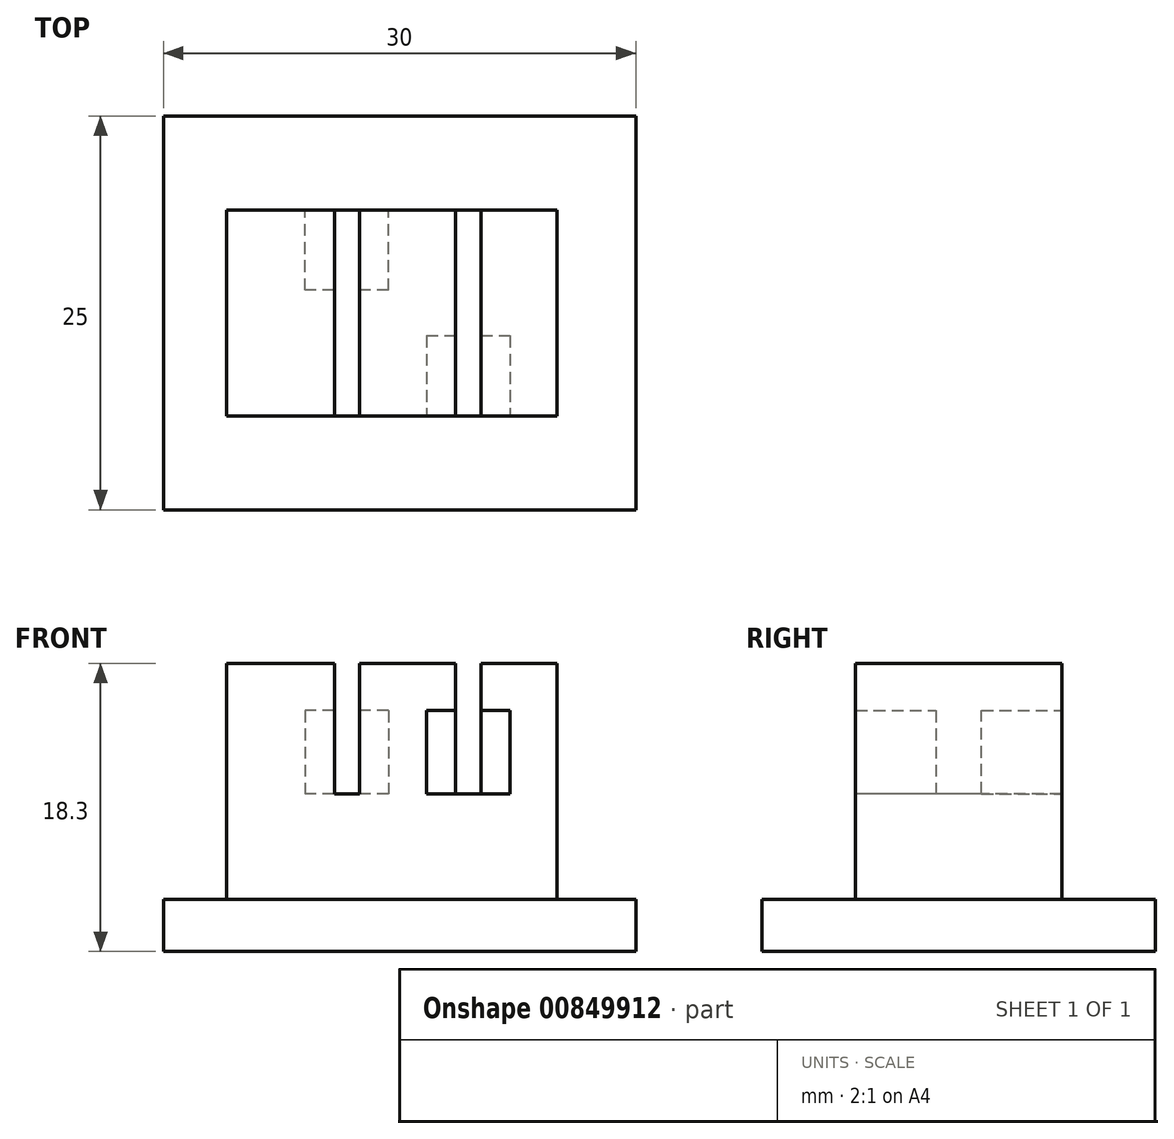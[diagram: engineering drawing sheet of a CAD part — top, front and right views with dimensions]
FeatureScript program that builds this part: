
annotation { "Feature Type Name" : "Feature", "Feature Type Description" : "" }
export const myFeature = defineFeature(function(context is Context, id is Id, definition is map)
    precondition{}
    {
        {
            var Q0;
            Q0=qCreatedBy(makeId("Top.planeOp"),FACE);
            var sketch = newSketch(context, id + "F0", { "sketchPlane" : qUnion([Q0])});
            skLineSegment(sketch, "E0.bottom", {"start": v(-15, 12.5) * mm, "end": v(15, 12.5) * mm});
            skLineSegment(sketch, "E0.top", {"start": v(-15, -12.5) * mm, "end": v(15, -12.5) * mm});
            skLineSegment(sketch, "E0.left", {"start": v(-15, 12.5) * mm, "end": v(-15, -12.5) * mm});
            skLineSegment(sketch, "E0.right", {"start": v(15, 12.5) * mm, "end": v(15, -12.5) * mm});
            skSolve(sketch);
        }
        {
            var Q0;
            Q0=makeQuery(id+"F0.imprint","IMPRINT",FACE,{"disambiguationData":[TD([[makeQuery(id+"F0.imprint","IMPRINT",EDGE,{"derivedFrom":sQuery(id+"F0.wireOp",EDGE,"E0.bottom")}),-1.0]])]});
            var Q1;
            Q1 = qSketchRegion(id + "F2", true);
            extrude(context, id + "F1", {"entities" : qUnion([Q0, Q1]), "depth" : 3.3 * mm, "offsetDistance" : 25 * mm});
        }
        {
            var Q0;
            Q0=makeQuery(id+"F1.opExtrude","CAP_FACE",FACE,{"disambiguationData":[OSD([sQuery(id+"F0.wireOp",EDGE,"E0.bottom"),sQuery(id+"F0.wireOp",EDGE,"E0.top"),sQuery(id+"F0.wireOp",EDGE,"E0.left"),sQuery(id+"F0.wireOp",EDGE,"E0.right")])],"isStart":false});
            var sketch = newSketch(context, id + "F2", { "sketchPlane" : qUnion([Q0])});
            skLineSegment(sketch, "E1.bottom", {"start": v(-11, 6.55) * mm, "end": v(10, 6.55) * mm});
            skLineSegment(sketch, "E1.top", {"start": v(-11, -6.55) * mm, "end": v(10, -6.55) * mm});
            skLineSegment(sketch, "E1.left", {"start": v(-11, 6.55) * mm, "end": v(-11, -6.55) * mm});
            skLineSegment(sketch, "E1.right", {"start": v(10, 6.55) * mm, "end": v(10, -6.55) * mm});
            skLineSegment(sketch, "E2", {"start": v(-11, -6.55) * mm, "end": v(-15, -6.55) * mm});
            skLineSegment(sketch, "E3", {"start": v(10, 6.55) * mm, "end": v(10, 12.5) * mm});
            skLineSegment(sketch, "E4", {"start": v(-11, -6.55) * mm, "end": v(-11, -12.5) * mm});
            skSolve(sketch);
        }
        {
            var Q0;
            Q0=makeQuery(id+"F2.imprint","IMPRINT",FACE,{"disambiguationData":[TD([[makeQuery(id+"F2.imprint","IMPRINT",EDGE,{"derivedFrom":sQuery(id+"F2.wireOp",EDGE,"E1.bottom")}),-1.0]])]});
            extrude(context, id + "F3", {"entities" : qUnion([Q0]), "operationType" : NewBodyOperationType.ADD, "depth" : 15 * mm, "offsetDistance" : 25 * mm});
        }
        {
            var Q0;
            Q0=makeQuery(id+"F3.opExtrude","SWEPT_FACE",FACE,{"disambiguationData":[OSD([sQuery(id+"F2.wireOp",EDGE,"E1.top")])]});
            var sketch = newSketch(context, id + "F4", { "sketchPlane" : qUnion([Q0])});
            skLineSegment(sketch, "E5.bottom", {"start": v(1.7, 15.3) * mm, "end": v(7, 15.3) * mm});
            skLineSegment(sketch, "E5.top", {"start": v(1.7, 10) * mm, "end": v(7, 10) * mm});
            skLineSegment(sketch, "E5.left", {"start": v(1.7, 15.3) * mm, "end": v(1.7, 10) * mm});
            skLineSegment(sketch, "E5.right", {"start": v(7, 15.3) * mm, "end": v(7, 10) * mm});
            skLineSegment(sketch, "E6", {"start": v(1.7, 15.3) * mm, "end": v(1.7, 18.3) * mm});
            skLineSegment(sketch, "E7", {"start": v(7, 15.3) * mm, "end": v(10, 15.3) * mm});
            skSolve(sketch);
        }
        {
            var Q0;
            Q0 = qSketchRegion(id + "F4", true);
            var Q1;
            Q1=makeQuery(id+"F4.imprint","IMPRINT",FACE,{"disambiguationData":[TD([[makeQuery(id+"F4.imprint","IMPRINT",EDGE,{"derivedFrom":sQuery(id+"F4.wireOp",EDGE,"E5.bottom")}),-1.0]])]});
            extrude(context, id + "F5", {"entities" : qUnion([Q0, Q1]), "operationType" : NewBodyOperationType.REMOVE, "oppositeDirection" : true, "depth" : 5.1 * mm, "offsetDistance" : 25 * mm});
        }
        {
            var Q0;
            Q0=makeQuery(id+"F3.opExtrude","CAP_FACE",FACE,{"disambiguationData":[OSD([sQuery(id+"F2.wireOp",EDGE,"E1.bottom"),sQuery(id+"F2.wireOp",EDGE,"E1.top"),sQuery(id+"F2.wireOp",EDGE,"E1.left"),sQuery(id+"F2.wireOp",EDGE,"E1.right")])],"isStart":false});
            var sketch = newSketch(context, id + "F6", { "sketchPlane" : qUnion([Q0])});
            skLineSegment(sketch, "E8.bottom", {"start": v(3.55, 6.55) * mm, "end": v(5.15, 6.55) * mm});
            skLineSegment(sketch, "E8.top", {"start": v(3.55, -6.55) * mm, "end": v(5.15, -6.55) * mm});
            skLineSegment(sketch, "E8.left", {"start": v(3.55, 6.55) * mm, "end": v(3.55, -6.55) * mm});
            skLineSegment(sketch, "E8.right", {"start": v(5.15, 6.55) * mm, "end": v(5.15, -6.55) * mm});
            skLineSegment(sketch, "E9", {"start": v(5.15, -6.55) * mm, "end": v(10, -6.55) * mm});
            skSolve(sketch);
        }
        {
            var Q0;
            Q0=makeQuery(id+"F6.imprint","IMPRINT",FACE,{"disambiguationData":[TD([[makeQuery(id+"F6.imprint","IMPRINT",EDGE,{"derivedFrom":sQuery(id+"F6.wireOp",EDGE,"E8.bottom")}),-1.0]])]});
            extrude(context, id + "F7", {"entities" : qUnion([Q0]), "operationType" : NewBodyOperationType.REMOVE, "oppositeDirection" : true, "depth" : 8.3 * mm, "offsetDistance" : 25 * mm});
        }
        {
            var Q0;
            Q0=makeQuery(id+"F3.opExtrude","SWEPT_FACE",FACE,{"disambiguationData":[OSD([sQuery(id+"F2.wireOp",EDGE,"E1.bottom")])]});
            var sketch = newSketch(context, id + "F8", { "sketchPlane" : qUnion([Q0])});
            skLineSegment(sketch, "E10.bottom", {"start": v(0.7, 15.3) * mm, "end": v(6, 15.3) * mm});
            skLineSegment(sketch, "E10.top", {"start": v(0.7, 10) * mm, "end": v(6, 10) * mm});
            skLineSegment(sketch, "E10.left", {"start": v(0.7, 15.3) * mm, "end": v(0.7, 10) * mm});
            skLineSegment(sketch, "E10.right", {"start": v(6, 15.3) * mm, "end": v(6, 10) * mm});
            skLineSegment(sketch, "E11", {"start": v(6, 15.3) * mm, "end": v(11, 15.3) * mm});
            skLineSegment(sketch, "E12", {"start": v(6, 15.3) * mm, "end": v(6, 18.3) * mm});
            skSolve(sketch);
        }
        {
            var Q0;
            Q0=makeQuery(id+"F8.imprint","IMPRINT",FACE,{"disambiguationData":[TD([[makeQuery(id+"F8.imprint","IMPRINT",EDGE,{"derivedFrom":sQuery(id+"F8.wireOp",EDGE,"E10.bottom")}),-1.0]])]});
            extrude(context, id + "F9", {"entities" : qUnion([Q0]), "operationType" : NewBodyOperationType.REMOVE, "oppositeDirection" : true, "depth" : 5.1 * mm, "offsetDistance" : 25 * mm});
        }
        {
            var Q0;
            {var subQ0=sQuery(id+"F2.wireOp",EDGE,"E1.bottom");var subQ1=sQuery(id+"F2.wireOp",EDGE,"E1.top");var subQ2=sQuery(id+"F2.wireOp",EDGE,"E1.left");Q0=makeQuery(id+"F7.boolean.opBoolean","SPLIT",FACE,{"disambiguationData":[TD([makeQuery(id+"F3.opExtrude","SWEPT_FACE",FACE,{"disambiguationData":[OSD([subQ2])]})])],"derivedFrom":makeQuery(id+"F3.opExtrude","CAP_FACE",FACE,{"disambiguationData":[OSD([subQ0,subQ1,subQ2,sQuery(id+"F2.wireOp",EDGE,"E1.right")])],"isStart":false})});}
            var sketch = newSketch(context, id + "F10", { "sketchPlane" : qUnion([Q0])});
            skLineSegment(sketch, "E13.bottom", {"start": v(-2.55, 6.55) * mm, "end": v(-4.15, 6.55) * mm});
            skLineSegment(sketch, "E13.top", {"start": v(-2.55, -6.55) * mm, "end": v(-4.15, -6.55) * mm});
            skLineSegment(sketch, "E13.left", {"start": v(-2.55, 6.55) * mm, "end": v(-2.55, -6.55) * mm});
            skLineSegment(sketch, "E13.right", {"start": v(-4.15, 6.55) * mm, "end": v(-4.15, -6.55) * mm});
            skLineSegment(sketch, "E14", {"start": v(-4.15, 6.55) * mm, "end": v(-11, 6.55) * mm});
            skSolve(sketch);
        }
        {
            var Q0;
            Q0=makeQuery(id+"F10.imprint","IMPRINT",FACE,{"disambiguationData":[TD([[makeQuery(id+"F10.imprint","IMPRINT",EDGE,{"derivedFrom":sQuery(id+"F10.wireOp",EDGE,"E13.bottom")}),-1.0]])]});
            extrude(context, id + "F11", {"entities" : qUnion([Q0]), "operationType" : NewBodyOperationType.REMOVE, "oppositeDirection" : true, "depth" : 8.3 * mm, "offsetDistance" : 25 * mm});
        }
    });
